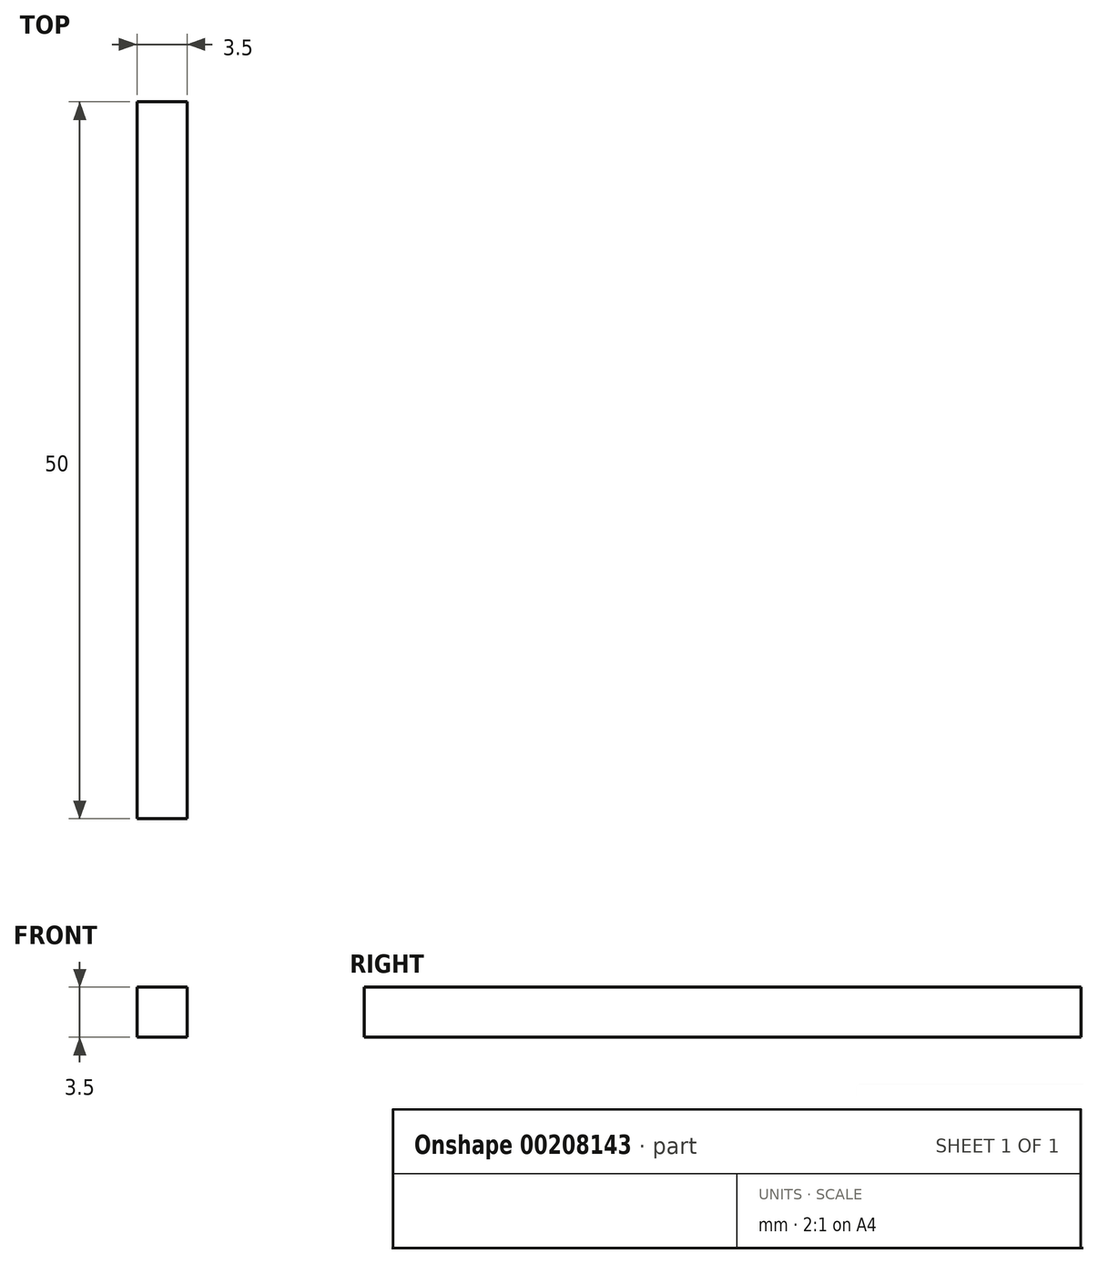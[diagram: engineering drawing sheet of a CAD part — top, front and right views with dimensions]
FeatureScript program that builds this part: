
annotation { "Feature Type Name" : "Feature", "Feature Type Description" : "" }
export const myFeature = defineFeature(function(context is Context, id is Id, definition is map)
    precondition{}
    {
        {
            var Q0;
            Q0=qCreatedBy(makeId("Top.planeOp"),FACE);
            var sketch = newSketch(context, id + "F0", { "sketchPlane" : qUnion([Q0])});
            skLineSegment(sketch, "E0.bottom", {"start": v(1.75, -25) * mm, "end": v(-1.75, -25) * mm});
            skLineSegment(sketch, "E0.top", {"start": v(1.75, 25) * mm, "end": v(-1.75, 25) * mm});
            skLineSegment(sketch, "E0.left", {"start": v(1.75, -25) * mm, "end": v(1.75, 25) * mm});
            skLineSegment(sketch, "E0.right", {"start": v(-1.75, -25) * mm, "end": v(-1.75, 25) * mm});
            skPoint(sketch, "E0.middle", {"position": v(0, 0) * mm});
            skSolve(sketch);
        }
        {
            var Q0;
            Q0 = qSketchRegion(id + "F0", true);
            extrude(context, id + "F1", {"entities" : qUnion([Q0]), "depth" : 3.5 * mm});
        }
    });
